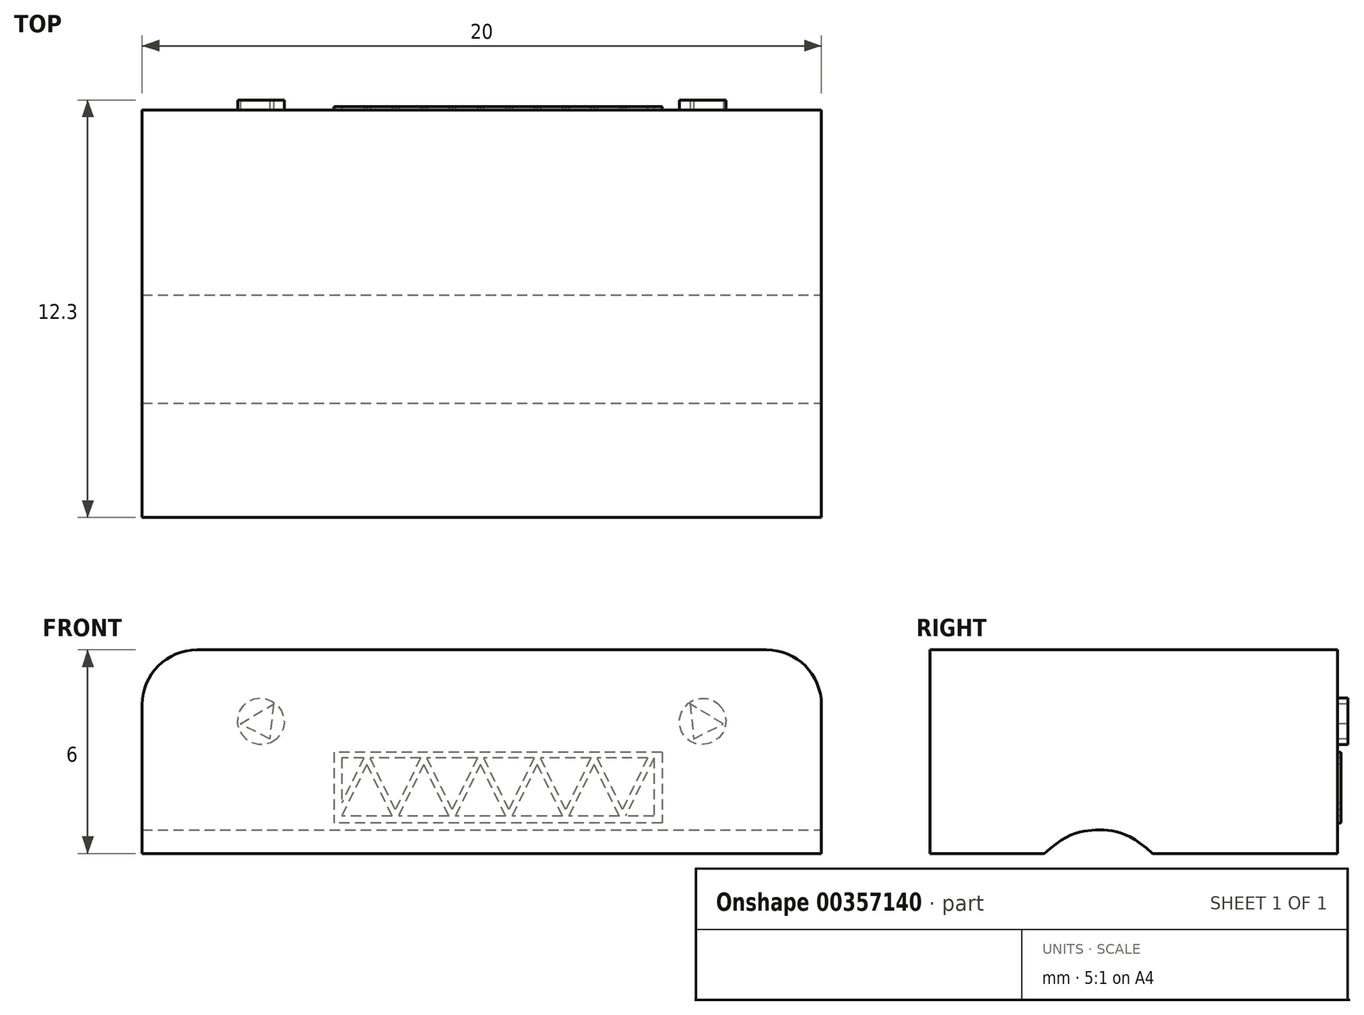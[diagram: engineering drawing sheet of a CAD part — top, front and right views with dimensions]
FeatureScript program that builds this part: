
annotation { "Feature Type Name" : "Feature", "Feature Type Description" : "" }
export const myFeature = defineFeature(function(context is Context, id is Id, definition is map)
    precondition{}
    {
        {
            var Q0;
            Q0=qCreatedBy(makeId("Top.planeOp"),FACE);
            var sketch = newSketch(context, id + "F0", { "sketchPlane" : qUnion([Q0])});
            skLineSegment(sketch, "E0.bottom", {"start": v(10, 6) * mm, "end": v(-10, 6) * mm});
            skLineSegment(sketch, "E0.top", {"start": v(10, -6) * mm, "end": v(-10, -6) * mm});
            skLineSegment(sketch, "E0.left", {"start": v(10, 6) * mm, "end": v(10, -6) * mm});
            skLineSegment(sketch, "E0.right", {"start": v(-10, 6) * mm, "end": v(-10, -6) * mm});
            skPoint(sketch, "E0.middle", {"position": v(0, 0) * mm});
            skSolve(sketch);
        }
        {
            var Q0;
            Q0 = qSketchRegion(id + "F0", true);
            extrude(context, id + "F1", {"entities" : qUnion([Q0]), "depth" : 6 * mm});
        }
        {
            var Q0;
            Q0=makeQuery(id+"F1.opExtrude","CAP_EDGE",EDGE,{"disambiguationData":[OSD([sQuery(id+"F0.wireOp",EDGE,"E0.left")])],"isStart":false});
            var Q1;
            Q1=makeQuery(id+"F1.opExtrude","CAP_EDGE",EDGE,{"disambiguationData":[OSD([sQuery(id+"F0.wireOp",EDGE,"E0.right")])],"isStart":false});
            fillet(context, id + "F2", {"entities" : qUnion([Q0, Q1]), "radius" : 1.62 * mm, "tangentPropagation" : true, "allowEdgeOverflow" : false});
        }
        {
            var Q0;
            Q0=makeQuery(id+"F1.opExtrude","SWEPT_FACE",FACE,{"disambiguationData":[OSD([sQuery(id+"F0.wireOp",EDGE,"E0.bottom")])]});
            var sketch = newSketch(context, id + "F3", { "sketchPlane" : qUnion([Q0])});
            skEllipse(sketch, "E1", {"center": v(-6.5, 3.9) * mm, "majorRadius": 0.68 * mm, "minorRadius": 0.7 * mm, "majorAxis": v(0.76, 0.65)});
            skEllipse(sketch, "E2.MirrorC", {"center": v(6.5, 3.9) * mm, "majorRadius": 0.68 * mm, "minorRadius": 0.7 * mm, "majorAxis": v(-0.76, 0.65)});
            skLineSegment(sketch, "E3.0", {"start": v(-6.13, 4.4) * mm, "end": v(-6.24, 3.38) * mm});
            skLineSegment(sketch, "E3.1", {"start": v(-6.24, 3.38) * mm, "end": v(-7.11, 3.82) * mm});
            skLineSegment(sketch, "E3.2", {"start": v(-7.11, 3.82) * mm, "end": v(-6.13, 4.4) * mm});
            skPoint(sketch, "E3.0.midPoint", {"position": v(-6.19, 3.9) * mm});
            skLineSegment(sketch, "E4.MirrorCS", {"start": v(7.11, 3.82) * mm, "end": v(6.13, 4.4) * mm});
            skLineSegment(sketch, "E5.MirrorCS", {"start": v(6.13, 4.4) * mm, "end": v(6.24, 3.38) * mm});
            skLineSegment(sketch, "E6.MirrorCS", {"start": v(6.24, 3.38) * mm, "end": v(7.11, 3.82) * mm});
            skSolve(sketch);
        }
        {
            var Q0;
            Q0 = qSketchRegion(id + "F3", true);
            extrude(context, id + "F4", {"entities" : qUnion([Q0]), "operationType" : NewBodyOperationType.ADD, "depth" : 0.3 * mm});
        }
        {
            var Q0;
            Q0=makeQuery(id+"F1.opExtrude","SWEPT_FACE",FACE,{"disambiguationData":[OSD([sQuery(id+"F0.wireOp",EDGE,"E0.bottom")])]});
            var sketch = newSketch(context, id + "F5", { "sketchPlane" : qUnion([Q0])});
            skLineSegment(sketch, "E7.bottom", {"start": v(-5.3, 2.97) * mm, "end": v(4.36, 2.97) * mm});
            skLineSegment(sketch, "E7.top", {"start": v(-5.3, 0.9) * mm, "end": v(4.36, 0.9) * mm});
            skLineSegment(sketch, "E7.left", {"start": v(-5.3, 2.97) * mm, "end": v(-5.3, 0.9) * mm});
            skLineSegment(sketch, "E7.right", {"start": v(4.36, 2.97) * mm, "end": v(4.36, 0.9) * mm});
            skLineSegment(sketch, "E8.bottom", {"start": v(-5.07, 2.81) * mm, "end": v(4.13, 2.81) * mm});
            skLineSegment(sketch, "E8.top", {"start": v(-5.07, 1.1) * mm, "end": v(4.13, 1.1) * mm});
            skLineSegment(sketch, "E8.left", {"start": v(-5.07, 2.81) * mm, "end": v(-5.07, 1.1) * mm});
            skLineSegment(sketch, "E8.right", {"start": v(4.13, 2.81) * mm, "end": v(4.13, 1.1) * mm});
            skLineSegment(sketch, "E9", {"start": v(-5.07, 2.81) * mm, "end": v(-4.23, 1.1) * mm});
            skLineSegment(sketch, "E10", {"start": v(-4.23, 1.1) * mm, "end": v(-3.4, 2.81) * mm});
            skLineSegment(sketch, "E11", {"start": v(-3.4, 2.81) * mm, "end": v(-2.56, 1.1) * mm});
            skLineSegment(sketch, "E12", {"start": v(-2.56, 1.1) * mm, "end": v(-1.73, 2.81) * mm});
            skLineSegment(sketch, "E13", {"start": v(-1.73, 2.81) * mm, "end": v(-0.89, 1.1) * mm});
            skLineSegment(sketch, "E14", {"start": v(-0.89, 1.1) * mm, "end": v(-0.05, 2.81) * mm});
            skLineSegment(sketch, "E15", {"start": v(-0.05, 2.81) * mm, "end": v(0.78, 1.1) * mm});
            skLineSegment(sketch, "E16", {"start": v(0.78, 1.1) * mm, "end": v(1.62, 2.81) * mm});
            skLineSegment(sketch, "E17", {"start": v(1.62, 2.81) * mm, "end": v(2.45, 1.1) * mm});
            skLineSegment(sketch, "E18", {"start": v(2.45, 1.1) * mm, "end": v(3.3, 2.81) * mm});
            skLineSegment(sketch, "E19", {"start": v(3.3, 2.81) * mm, "end": v(4.13, 1.1) * mm});
            skLineSegment(sketch, "E20", {"start": v(-4.89, 2.81) * mm, "end": v(-4.05, 1.1) * mm});
            skLineSegment(sketch, "E21", {"start": v(-4.05, 1.1) * mm, "end": v(-3.21, 2.81) * mm});
            skLineSegment(sketch, "E22", {"start": v(-3.21, 2.81) * mm, "end": v(-2.38, 1.1) * mm});
            skLineSegment(sketch, "E23", {"start": v(-2.38, 1.1) * mm, "end": v(-1.54, 2.81) * mm});
            skLineSegment(sketch, "E24", {"start": v(-1.54, 2.81) * mm, "end": v(-0.7, 1.1) * mm});
            skLineSegment(sketch, "E25", {"start": v(-0.7, 1.1) * mm, "end": v(0.13, 2.81) * mm});
            skLineSegment(sketch, "E26", {"start": v(0.13, 2.81) * mm, "end": v(0.97, 1.1) * mm});
            skLineSegment(sketch, "E27", {"start": v(0.97, 1.1) * mm, "end": v(1.8, 2.81) * mm});
            skLineSegment(sketch, "E28", {"start": v(1.8, 2.81) * mm, "end": v(2.64, 1.1) * mm});
            skLineSegment(sketch, "E29", {"start": v(2.64, 1.1) * mm, "end": v(3.47, 2.81) * mm});
            skLineSegment(sketch, "E30", {"start": v(3.47, 2.81) * mm, "end": v(4.13, 1.48) * mm});
            skSolve(sketch);
        }
        {
            var Q0;
            Q0 = qSketchRegion(id + "F5", true);
            var Q1;
            {var subQ0=sQuery(id+"F5.wireOp",EDGE,"E9");Q1=makeQuery(id+"F5.imprint","IMPRINT",FACE,{"disambiguationData":[TD([[makeQuery(id+"F5.imprint","IMPRINT",EDGE,{"derivedFrom":subQ0}),1.0]])]});}
            var Q2;
            {var subQ1=sQuery(id+"F5.wireOp",EDGE,"E10");var subQ3=sQuery(id+"F5.wireOp",EDGE,"E20");var subQ4=makeQuery(id+"F5.imprint","INTERSECT",VERTEX,{"derivedFrom":[subQ1,subQ3]});Q2=makeQuery(id+"F5.imprint","IMPRINT",FACE,{"disambiguationData":[TD([[makeQuery(id+"F5.imprint","IMPRINT",EDGE,{"disambiguationData":[TD([[subQ4,-1.0]])],"derivedFrom":subQ1}),-1.0]])]});}
            var Q3;
            {var subQ1=sQuery(id+"F5.wireOp",EDGE,"E11");var subQ3=sQuery(id+"F5.wireOp",EDGE,"E21");var subQ4=makeQuery(id+"F5.imprint","INTERSECT",VERTEX,{"derivedFrom":[subQ1,subQ3]});Q3=makeQuery(id+"F5.imprint","IMPRINT",FACE,{"disambiguationData":[TD([[makeQuery(id+"F5.imprint","IMPRINT",EDGE,{"disambiguationData":[TD([[subQ4,-1.0]])],"derivedFrom":subQ1}),1.0]])]});}
            var Q4;
            {var subQ1=sQuery(id+"F5.wireOp",EDGE,"E12");var subQ3=sQuery(id+"F5.wireOp",EDGE,"E22");var subQ4=makeQuery(id+"F5.imprint","INTERSECT",VERTEX,{"derivedFrom":[subQ1,subQ3]});Q4=makeQuery(id+"F5.imprint","IMPRINT",FACE,{"disambiguationData":[TD([[makeQuery(id+"F5.imprint","IMPRINT",EDGE,{"disambiguationData":[TD([[subQ4,-1.0]])],"derivedFrom":subQ1}),-1.0]])]});}
            var Q5;
            {var subQ1=sQuery(id+"F5.wireOp",EDGE,"E13");var subQ3=sQuery(id+"F5.wireOp",EDGE,"E23");var subQ4=makeQuery(id+"F5.imprint","INTERSECT",VERTEX,{"derivedFrom":[subQ1,subQ3]});Q5=makeQuery(id+"F5.imprint","IMPRINT",FACE,{"disambiguationData":[TD([[makeQuery(id+"F5.imprint","IMPRINT",EDGE,{"disambiguationData":[TD([[subQ4,-1.0]])],"derivedFrom":subQ1}),1.0]])]});}
            var Q6;
            {var subQ1=sQuery(id+"F5.wireOp",EDGE,"E14");var subQ3=sQuery(id+"F5.wireOp",EDGE,"E24");var subQ4=makeQuery(id+"F5.imprint","INTERSECT",VERTEX,{"derivedFrom":[subQ1,subQ3]});Q6=makeQuery(id+"F5.imprint","IMPRINT",FACE,{"disambiguationData":[TD([[makeQuery(id+"F5.imprint","IMPRINT",EDGE,{"disambiguationData":[TD([[subQ4,-1.0]])],"derivedFrom":subQ1}),-1.0]])]});}
            var Q7;
            {var subQ1=sQuery(id+"F5.wireOp",EDGE,"E15");var subQ3=sQuery(id+"F5.wireOp",EDGE,"E25");var subQ4=makeQuery(id+"F5.imprint","INTERSECT",VERTEX,{"derivedFrom":[subQ1,subQ3]});Q7=makeQuery(id+"F5.imprint","IMPRINT",FACE,{"disambiguationData":[TD([[makeQuery(id+"F5.imprint","IMPRINT",EDGE,{"disambiguationData":[TD([[subQ4,-1.0]])],"derivedFrom":subQ1}),1.0]])]});}
            var Q8;
            {var subQ1=sQuery(id+"F5.wireOp",EDGE,"E16");var subQ3=sQuery(id+"F5.wireOp",EDGE,"E26");var subQ4=makeQuery(id+"F5.imprint","INTERSECT",VERTEX,{"derivedFrom":[subQ1,subQ3]});Q8=makeQuery(id+"F5.imprint","IMPRINT",FACE,{"disambiguationData":[TD([[makeQuery(id+"F5.imprint","IMPRINT",EDGE,{"disambiguationData":[TD([[subQ4,-1.0]])],"derivedFrom":subQ1}),-1.0]])]});}
            var Q9;
            {var subQ1=sQuery(id+"F5.wireOp",EDGE,"E17");var subQ3=sQuery(id+"F5.wireOp",EDGE,"E27");var subQ4=makeQuery(id+"F5.imprint","INTERSECT",VERTEX,{"derivedFrom":[subQ1,subQ3]});Q9=makeQuery(id+"F5.imprint","IMPRINT",FACE,{"disambiguationData":[TD([[makeQuery(id+"F5.imprint","IMPRINT",EDGE,{"disambiguationData":[TD([[subQ4,-1.0]])],"derivedFrom":subQ1}),1.0]])]});}
            var Q10;
            {var subQ1=sQuery(id+"F5.wireOp",EDGE,"E18");var subQ3=sQuery(id+"F5.wireOp",EDGE,"E28");var subQ4=makeQuery(id+"F5.imprint","INTERSECT",VERTEX,{"derivedFrom":[subQ1,subQ3]});Q10=makeQuery(id+"F5.imprint","IMPRINT",FACE,{"disambiguationData":[TD([[makeQuery(id+"F5.imprint","IMPRINT",EDGE,{"disambiguationData":[TD([[subQ4,-1.0]])],"derivedFrom":subQ1}),-1.0]])]});}
            var Q11;
            {var subQ3=sQuery(id+"F5.wireOp",EDGE,"E30");Q11=makeQuery(id+"F5.imprint","IMPRINT",FACE,{"disambiguationData":[TD([[makeQuery(id+"F5.imprint","IMPRINT",EDGE,{"derivedFrom":subQ3}),-1.0]])]});}
            var Q12;
            {var subQ0=sQuery(id+"F5.wireOp",EDGE,"E10");var subQ3=sQuery(id+"F5.wireOp",EDGE,"E20");var subQ5=makeQuery(id+"F5.imprint","INTERSECT",VERTEX,{"derivedFrom":[subQ0,subQ3]});Q12=makeQuery(id+"F5.imprint","IMPRINT",FACE,{"disambiguationData":[TD([[makeQuery(id+"F5.imprint","IMPRINT",EDGE,{"disambiguationData":[TD([[subQ5,1.0]])],"derivedFrom":subQ0}),-1.0]])]});}
            var Q13;
            {var subQ0=sQuery(id+"F5.wireOp",EDGE,"E11");var subQ3=sQuery(id+"F5.wireOp",EDGE,"E21");var subQ5=makeQuery(id+"F5.imprint","INTERSECT",VERTEX,{"derivedFrom":[subQ0,subQ3]});Q13=makeQuery(id+"F5.imprint","IMPRINT",FACE,{"disambiguationData":[TD([[makeQuery(id+"F5.imprint","IMPRINT",EDGE,{"disambiguationData":[TD([[subQ5,1.0]])],"derivedFrom":subQ0}),1.0]])]});}
            var Q14;
            {var subQ0=sQuery(id+"F5.wireOp",EDGE,"E12");var subQ3=sQuery(id+"F5.wireOp",EDGE,"E22");var subQ5=makeQuery(id+"F5.imprint","INTERSECT",VERTEX,{"derivedFrom":[subQ0,subQ3]});Q14=makeQuery(id+"F5.imprint","IMPRINT",FACE,{"disambiguationData":[TD([[makeQuery(id+"F5.imprint","IMPRINT",EDGE,{"disambiguationData":[TD([[subQ5,1.0]])],"derivedFrom":subQ0}),-1.0]])]});}
            var Q15;
            {var subQ0=sQuery(id+"F5.wireOp",EDGE,"E13");var subQ3=sQuery(id+"F5.wireOp",EDGE,"E23");var subQ5=makeQuery(id+"F5.imprint","INTERSECT",VERTEX,{"derivedFrom":[subQ0,subQ3]});Q15=makeQuery(id+"F5.imprint","IMPRINT",FACE,{"disambiguationData":[TD([[makeQuery(id+"F5.imprint","IMPRINT",EDGE,{"disambiguationData":[TD([[subQ5,1.0]])],"derivedFrom":subQ0}),1.0]])]});}
            var Q16;
            {var subQ0=sQuery(id+"F5.wireOp",EDGE,"E14");var subQ3=sQuery(id+"F5.wireOp",EDGE,"E24");var subQ5=makeQuery(id+"F5.imprint","INTERSECT",VERTEX,{"derivedFrom":[subQ0,subQ3]});Q16=makeQuery(id+"F5.imprint","IMPRINT",FACE,{"disambiguationData":[TD([[makeQuery(id+"F5.imprint","IMPRINT",EDGE,{"disambiguationData":[TD([[subQ5,1.0]])],"derivedFrom":subQ0}),-1.0]])]});}
            var Q17;
            {var subQ0=sQuery(id+"F5.wireOp",EDGE,"E15");var subQ3=sQuery(id+"F5.wireOp",EDGE,"E25");var subQ5=makeQuery(id+"F5.imprint","INTERSECT",VERTEX,{"derivedFrom":[subQ0,subQ3]});Q17=makeQuery(id+"F5.imprint","IMPRINT",FACE,{"disambiguationData":[TD([[makeQuery(id+"F5.imprint","IMPRINT",EDGE,{"disambiguationData":[TD([[subQ5,1.0]])],"derivedFrom":subQ0}),1.0]])]});}
            var Q18;
            {var subQ0=sQuery(id+"F5.wireOp",EDGE,"E16");var subQ3=sQuery(id+"F5.wireOp",EDGE,"E26");var subQ5=makeQuery(id+"F5.imprint","INTERSECT",VERTEX,{"derivedFrom":[subQ0,subQ3]});Q18=makeQuery(id+"F5.imprint","IMPRINT",FACE,{"disambiguationData":[TD([[makeQuery(id+"F5.imprint","IMPRINT",EDGE,{"disambiguationData":[TD([[subQ5,1.0]])],"derivedFrom":subQ0}),-1.0]])]});}
            var Q19;
            {var subQ0=sQuery(id+"F5.wireOp",EDGE,"E17");var subQ3=sQuery(id+"F5.wireOp",EDGE,"E27");var subQ5=makeQuery(id+"F5.imprint","INTERSECT",VERTEX,{"derivedFrom":[subQ0,subQ3]});Q19=makeQuery(id+"F5.imprint","IMPRINT",FACE,{"disambiguationData":[TD([[makeQuery(id+"F5.imprint","IMPRINT",EDGE,{"disambiguationData":[TD([[subQ5,1.0]])],"derivedFrom":subQ0}),1.0]])]});}
            var Q20;
            {var subQ0=sQuery(id+"F5.wireOp",EDGE,"E18");var subQ3=sQuery(id+"F5.wireOp",EDGE,"E28");var subQ5=makeQuery(id+"F5.imprint","INTERSECT",VERTEX,{"derivedFrom":[subQ0,subQ3]});Q20=makeQuery(id+"F5.imprint","IMPRINT",FACE,{"disambiguationData":[TD([[makeQuery(id+"F5.imprint","IMPRINT",EDGE,{"disambiguationData":[TD([[subQ5,1.0]])],"derivedFrom":subQ0}),-1.0]])]});}
            var Q21;
            {var subQ0=sQuery(id+"F5.wireOp",EDGE,"E19");var subQ3=sQuery(id+"F5.wireOp",EDGE,"E29");var subQ5=makeQuery(id+"F5.imprint","INTERSECT",VERTEX,{"derivedFrom":[subQ0,subQ3]});Q21=makeQuery(id+"F5.imprint","IMPRINT",FACE,{"disambiguationData":[TD([[makeQuery(id+"F5.imprint","IMPRINT",EDGE,{"disambiguationData":[TD([[subQ5,1.0]])],"derivedFrom":subQ0}),1.0]])]});}
            extrude(context, id + "F6", {"entities" : qUnion([Q0, Q1, Q2, Q3, Q4, Q5, Q6, Q7, Q8, Q9, Q10, Q11, Q12, Q13, Q14, Q15, Q16, Q17, Q18, Q19, Q20, Q21]), "operationType" : NewBodyOperationType.ADD, "depth" : .1 * mm});
        }
        {
            var Q0;
            Q0=makeQuery(id+"F1.opExtrude","SWEPT_FACE",FACE,{"disambiguationData":[OSD([sQuery(id+"F0.wireOp",EDGE,"E0.left")])]});
            var sketch = newSketch(context, id + "F7", { "sketchPlane" : qUnion([Q0])});
            skLineSegment(sketch, "E31", {"start": v(-2.63, 0) * mm, "end": v(0.55, 0) * mm});
            skFitSpline(sketch, "E32", {"points": [v(-2.63, 0) * mm, v(-1.07, 0.69) * mm, v(0.55, 0) * mm], "startDerivative": vector(4.12, 3.8) * mm, "endDerivative": vector(4.35, -3.93) * mm});
            skSolve(sketch);
        }
        {
            var Q0;
            Q0 = qSketchRegion(id + "F7", true);
            extrude(context, id + "F8", {"entities" : qUnion([Q0]), "operationType" : NewBodyOperationType.REMOVE, "oppositeDirection" : true, "depth" : 25 * mm});
        }
    });
